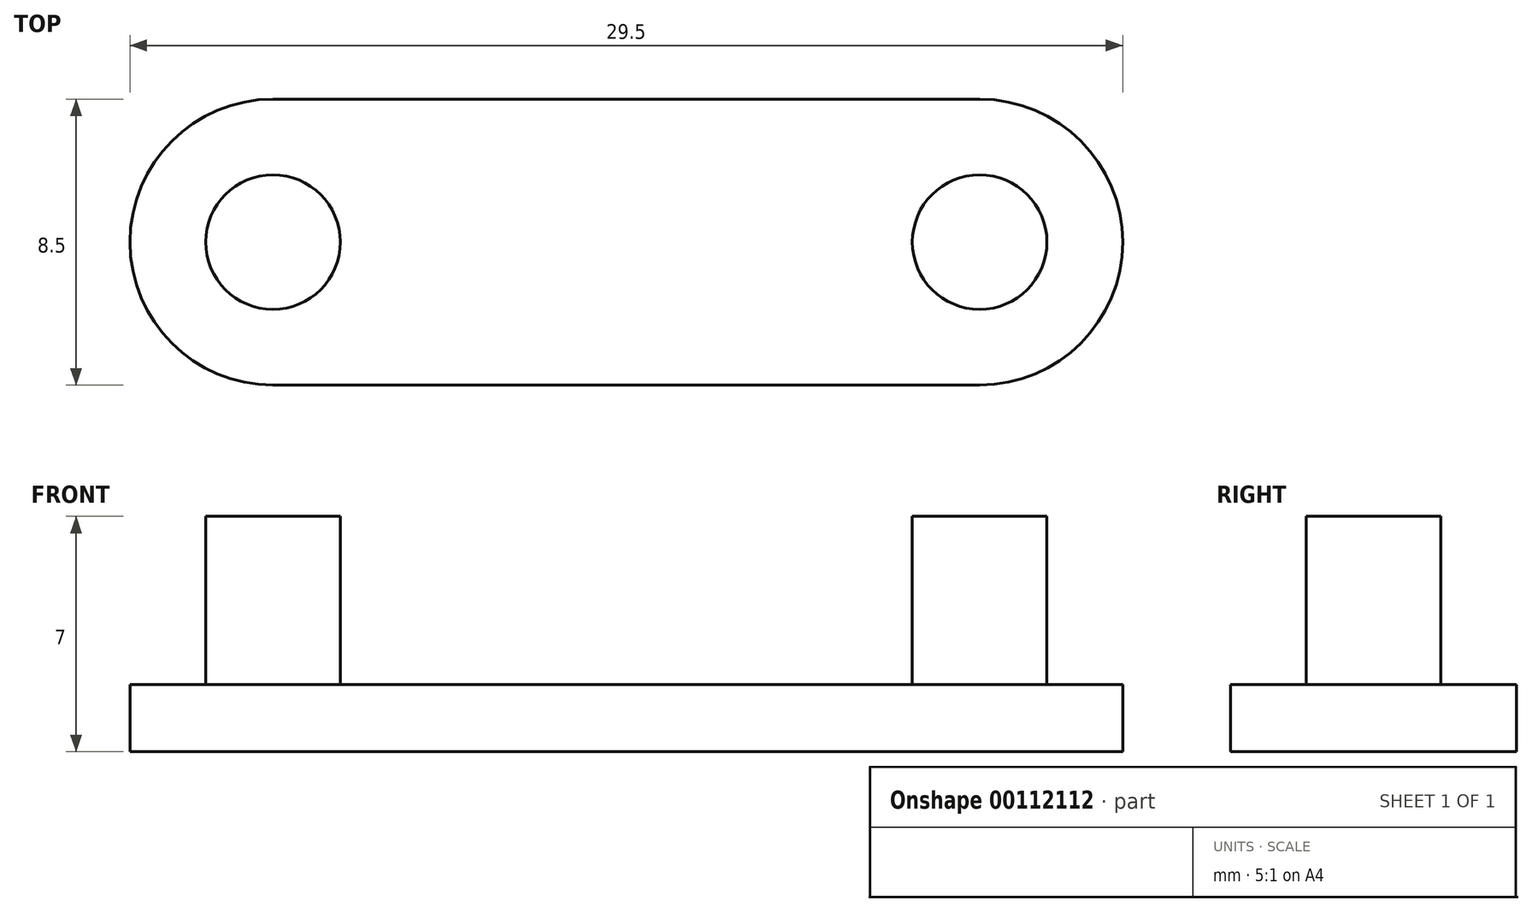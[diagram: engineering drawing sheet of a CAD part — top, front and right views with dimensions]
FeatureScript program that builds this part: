
annotation { "Feature Type Name" : "Feature", "Feature Type Description" : "" }
export const myFeature = defineFeature(function(context is Context, id is Id, definition is map)
    precondition{}
    {
        {
            var Q0;
            Q0=qCreatedBy(makeId("Top.planeOp"),FACE);
            var sketch = newSketch(context, id + "F0", { "sketchPlane" : qUnion([Q0])});
            skCircle(sketch, "E0", {"center": v(0, 0) * mm, "radius": 4.25 * mm});
            skCircle(sketch, "E1", {"center": v(21, 0) * mm, "radius": 4.25 * mm});
            skLineSegment(sketch, "E2", {"start": v(0, -4.25) * mm, "end": v(21, -4.25) * mm});
            skLineSegment(sketch, "E3", {"start": v(21, 4.25) * mm, "end": v(0, 4.25) * mm});
            skSolve(sketch);
        }
        {
            var Q0;
            Q0 = qSketchRegion(id + "F0", true);
            extrude(context, id + "F1", {"entities" : qUnion([Q0]), "depth" : 2 * mm});
        }
        {
            var Q0;
            Q0=makeQuery(id+"F1.opExtrude","CAP_FACE",FACE,{"disambiguationData":[OSD([sQuery(id+"F0.wireOp",EDGE,"E0"),sQuery(id+"F0.wireOp",EDGE,"E1"),sQuery(id+"F0.wireOp",EDGE,"E2"),sQuery(id+"F0.wireOp",EDGE,"E3")])],"isStart":false});
            var sketch = newSketch(context, id + "F2", { "sketchPlane" : qUnion([Q0])});
            skCircle(sketch, "E4", {"center": v(0, 0) * mm, "radius": 2 * mm});
            skLineSegment(sketch, "E5", {"start": v(10.5, 4.25) * mm, "end": v(10.5, -4.25) * mm});
            skCircle(sketch, "E6.MirrorC", {"center": v(21, 0) * mm, "radius": 2 * mm});
            skSolve(sketch);
        }
        {
            var Q0;
            Q0 = qSketchRegion(id + "F2", true);
            extrude(context, id + "F3", {"entities" : qUnion([Q0]), "operationType" : NewBodyOperationType.ADD, "depth" : 5 * mm});
        }
    });
